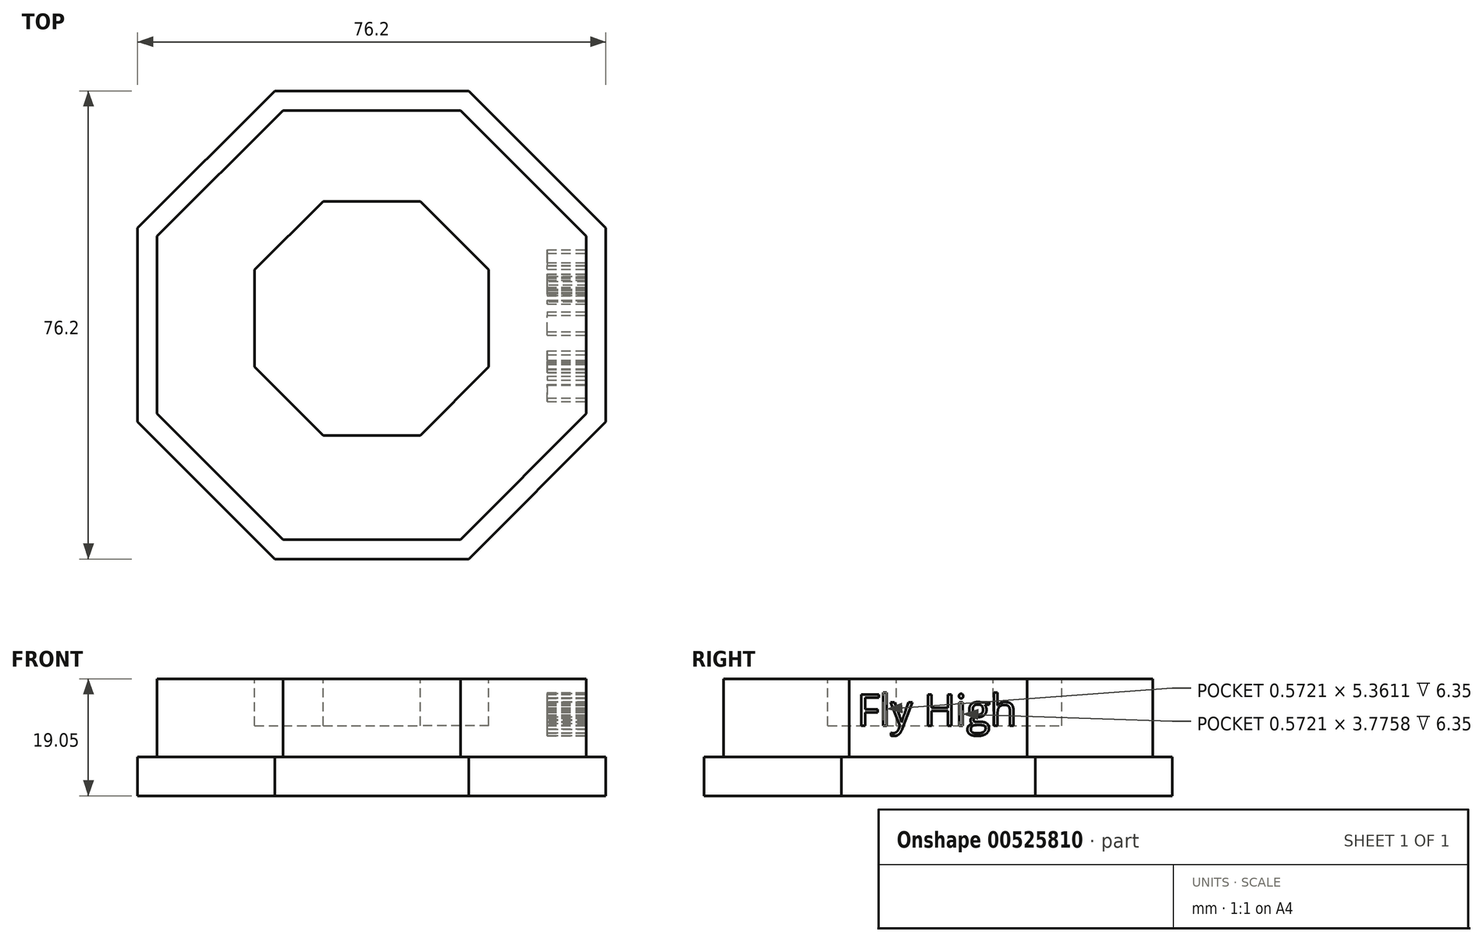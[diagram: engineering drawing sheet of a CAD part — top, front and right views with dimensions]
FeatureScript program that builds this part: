
annotation { "Feature Type Name" : "Feature", "Feature Type Description" : "" }
export const myFeature = defineFeature(function(context is Context, id is Id, definition is map)
    precondition{}
    {
        {
            var Q0;
            Q0=qCreatedBy(makeId("Top.planeOp"),FACE);
            var sketch = newSketch(context, id + "F0", { "sketchPlane" : qUnion([Q0])});
            skCircle(sketch, "E0.cCircle", {"center": v(0, 0) * mm, "radius": 38.1 * mm, "construction": true});
            skLineSegment(sketch, "E0.0", {"start": v(38.1, 15.78) * mm, "end": v(38.1, -15.78) * mm});
            skLineSegment(sketch, "E0.1", {"start": v(38.1, -15.78) * mm, "end": v(15.78, -38.1) * mm});
            skLineSegment(sketch, "E0.2", {"start": v(15.78, -38.1) * mm, "end": v(-15.78, -38.1) * mm});
            skLineSegment(sketch, "E0.3", {"start": v(-15.78, -38.1) * mm, "end": v(-38.1, -15.78) * mm});
            skLineSegment(sketch, "E0.4", {"start": v(-38.1, -15.78) * mm, "end": v(-38.1, 15.78) * mm});
            skLineSegment(sketch, "E0.5", {"start": v(-38.1, 15.78) * mm, "end": v(-15.78, 38.1) * mm});
            skLineSegment(sketch, "E0.6", {"start": v(-15.78, 38.1) * mm, "end": v(15.78, 38.1) * mm});
            skLineSegment(sketch, "E0.7", {"start": v(15.78, 38.1) * mm, "end": v(38.1, 15.78) * mm});
            skPoint(sketch, "E0.0.midPoint", {"position": v(38.1, 0) * mm});
            skSolve(sketch);
        }
        {
            var Q0;
            Q0 = qSketchRegion(id + "F0", true);
            extrude(context, id + "F1", {"entities" : qUnion([Q0]), "depth" : 6.35 * mm, "offsetDistance" : 25.4 * mm});
        }
        {
            var Q0;
            Q0=makeQuery(id+"F1.opExtrude","CAP_FACE",FACE,{"disambiguationData":[OSD([sQuery(id+"F0.wireOp",EDGE,"E0.0"),sQuery(id+"F0.wireOp",EDGE,"E0.1"),sQuery(id+"F0.wireOp",EDGE,"E0.2"),sQuery(id+"F0.wireOp",EDGE,"E0.3"),sQuery(id+"F0.wireOp",EDGE,"E0.4"),sQuery(id+"F0.wireOp",EDGE,"E0.5"),sQuery(id+"F0.wireOp",EDGE,"E0.6"),sQuery(id+"F0.wireOp",EDGE,"E0.7")])],"isStart":false});
            var sketch = newSketch(context, id + "F2", { "sketchPlane" : qUnion([Q0])});
            skCircle(sketch, "E1.cCircle", {"center": v(0, 0) * mm, "radius": 34.92 * mm, "construction": true});
            skLineSegment(sketch, "E1.0", {"start": v(-34.92, -14.47) * mm, "end": v(-34.92, 14.47) * mm});
            skLineSegment(sketch, "E1.1", {"start": v(-34.93, 14.47) * mm, "end": v(-14.47, 34.93) * mm});
            skLineSegment(sketch, "E1.2", {"start": v(-14.47, 34.92) * mm, "end": v(14.47, 34.92) * mm});
            skLineSegment(sketch, "E1.3", {"start": v(14.47, 34.92) * mm, "end": v(34.92, 14.47) * mm});
            skLineSegment(sketch, "E1.4", {"start": v(34.92, 14.47) * mm, "end": v(34.92, -14.47) * mm});
            skLineSegment(sketch, "E1.5", {"start": v(34.92, -14.47) * mm, "end": v(14.47, -34.92) * mm});
            skLineSegment(sketch, "E1.6", {"start": v(14.47, -34.92) * mm, "end": v(-14.47, -34.92) * mm});
            skLineSegment(sketch, "E1.7", {"start": v(-14.47, -34.92) * mm, "end": v(-34.92, -14.47) * mm});
            skPoint(sketch, "E1.0.midPoint", {"position": v(-34.92, 0) * mm});
            skSolve(sketch);
        }
        {
            var Q0;
            Q0=makeQuery(id+"F2.imprint","IMPRINT",FACE,{"disambiguationData":[TD([[makeQuery(id+"F2.imprint","IMPRINT",EDGE,{"derivedFrom":sQuery(id+"F2.wireOp",EDGE,"E1.0")}),-1.0]])]});
            extrude(context, id + "F3", {"entities" : qUnion([Q0]), "operationType" : NewBodyOperationType.ADD, "depth" : 12.7 * mm, "offsetDistance" : 25.4 * mm});
        }
        {
            var Q0;
            Q0=makeQuery(id+"F3.opExtrude","SWEPT_FACE",FACE,{"disambiguationData":[OSD([sQuery(id+"F2.wireOp",EDGE,"E1.4")])]});
            var sketch = newSketch(context, id + "F4", { "sketchPlane" : qUnion([Q0])});
            skText(sketch, "E2", { "text": "Fly High", "fontName": "OpenSans-Regular.ttf"});
            const initialGuessF4  = {"E2": [-0.0132, 0.01143, 1, 0, 0.00508]};
            skSetInitialGuess(sketch, initialGuessF4);
            skSolve(sketch);
        }
        {
            var Q0;
            Q0 = qSketchRegion(id + "F4", true);
            extrude(context, id + "F5", {"entities" : qUnion([Q0]), "operationType" : NewBodyOperationType.REMOVE, "oppositeDirection" : true, "depth" : 6.35 * mm, "offsetDistance" : 25.4 * mm});
        }
        {
            var Q0;
            Q0=makeQuery(id+"F3.opExtrude","CAP_FACE",FACE,{"disambiguationData":[OSD([sQuery(id+"F2.wireOp",EDGE,"E1.0"),sQuery(id+"F2.wireOp",EDGE,"E1.1"),sQuery(id+"F2.wireOp",EDGE,"E1.2"),sQuery(id+"F2.wireOp",EDGE,"E1.3"),sQuery(id+"F2.wireOp",EDGE,"E1.4"),sQuery(id+"F2.wireOp",EDGE,"E1.5"),sQuery(id+"F2.wireOp",EDGE,"E1.6"),sQuery(id+"F2.wireOp",EDGE,"E1.7")])],"isStart":false});
            var sketch = newSketch(context, id + "F6", { "sketchPlane" : qUnion([Q0])});
            skCircle(sketch, "E3.cCircle", {"center": v(0, 1.07) * mm, "radius": 19.05 * mm, "construction": true});
            skLineSegment(sketch, "E3.0", {"start": v(-7.9, 20.12) * mm, "end": v(7.9, 20.12) * mm});
            skLineSegment(sketch, "E3.1", {"start": v(7.9, 20.12) * mm, "end": v(19.05, 8.96) * mm});
            skLineSegment(sketch, "E3.2", {"start": v(19.05, 8.96) * mm, "end": v(19.05, -6.82) * mm});
            skLineSegment(sketch, "E3.3", {"start": v(19.05, -6.82) * mm, "end": v(7.9, -17.98) * mm});
            skLineSegment(sketch, "E3.4", {"start": v(7.9, -17.98) * mm, "end": v(-7.9, -17.98) * mm});
            skLineSegment(sketch, "E3.5", {"start": v(-7.9, -17.98) * mm, "end": v(-19.05, -6.82) * mm});
            skLineSegment(sketch, "E3.6", {"start": v(-19.05, -6.82) * mm, "end": v(-19.05, 8.96) * mm});
            skLineSegment(sketch, "E3.7", {"start": v(-19.05, 8.96) * mm, "end": v(-7.9, 20.12) * mm});
            skPoint(sketch, "E3.0.midPoint", {"position": v(0, 20.12) * mm});
            skSolve(sketch);
        }
        {
            var Q0;
            Q0 = qSketchRegion(id + "F6", true);
            extrude(context, id + "F7", {"entities" : qUnion([Q0]), "operationType" : NewBodyOperationType.REMOVE, "oppositeDirection" : true, "depth" : 7.62 * mm, "offsetDistance" : 25.4 * mm});
        }
    });
